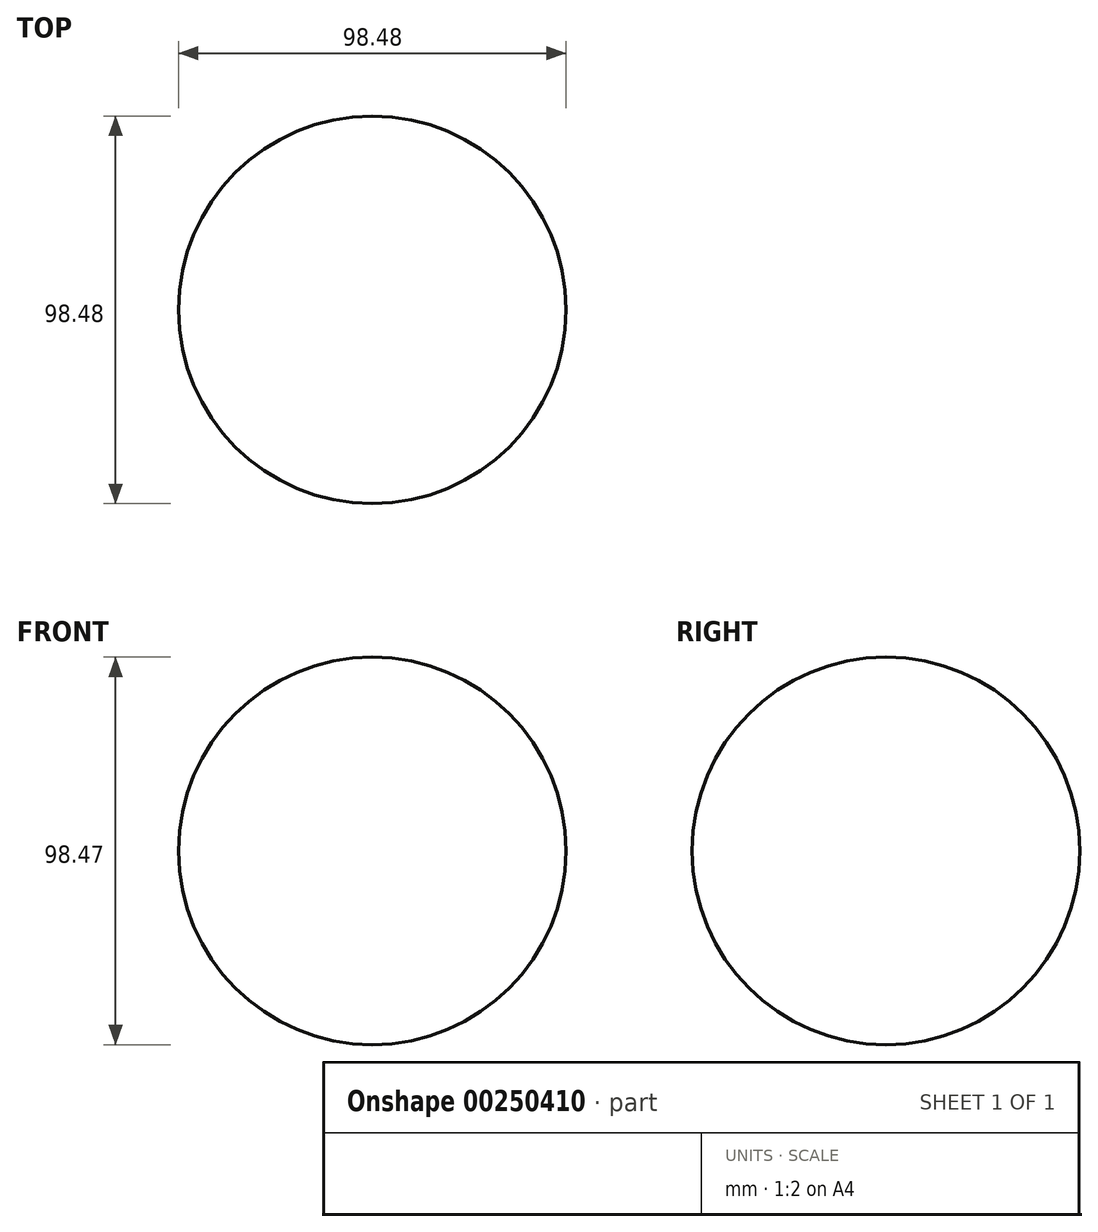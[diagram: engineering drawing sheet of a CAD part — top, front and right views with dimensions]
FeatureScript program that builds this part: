
annotation { "Feature Type Name" : "Feature", "Feature Type Description" : "" }
export const myFeature = defineFeature(function(context is Context, id is Id, definition is map)
    precondition{}
    {
        {
            var Q0;
            Q0=qCreatedBy(makeId("Front.planeOp"),FACE);
            var sketch = newSketch(context, id + "F0", { "sketchPlane" : qUnion([Q0])});
            skLineSegment(sketch, "E0", {"start": v(0, 0) * mm, "end": v(0, 98.47) * mm});
            skArc(sketch, "E1", {"start": v(0, 98.47) * mm, "mid": v(49.24, 49.24) * mm, "end": v(0, 0) * mm});
            skSolve(sketch);
        }
        {
            var Q0;
            Q0=makeQuery(id+"F0.imprint","IMPRINT",FACE,{"disambiguationData":[TD([[makeQuery(id+"F0.imprint","IMPRINT",EDGE,{"derivedFrom":sQuery(id+"F0.wireOp",EDGE,"E0")}),-1.0]])]});
            var Q1;
            Q1=sQuery(id+"F0.wireOp",EDGE,"E0");
            revolve(context, id + "F1", {"entities" : qUnion([Q0]), "axis" : qUnion([Q1]), "revolveType" : RevolveType.FULL});
        }
    });
